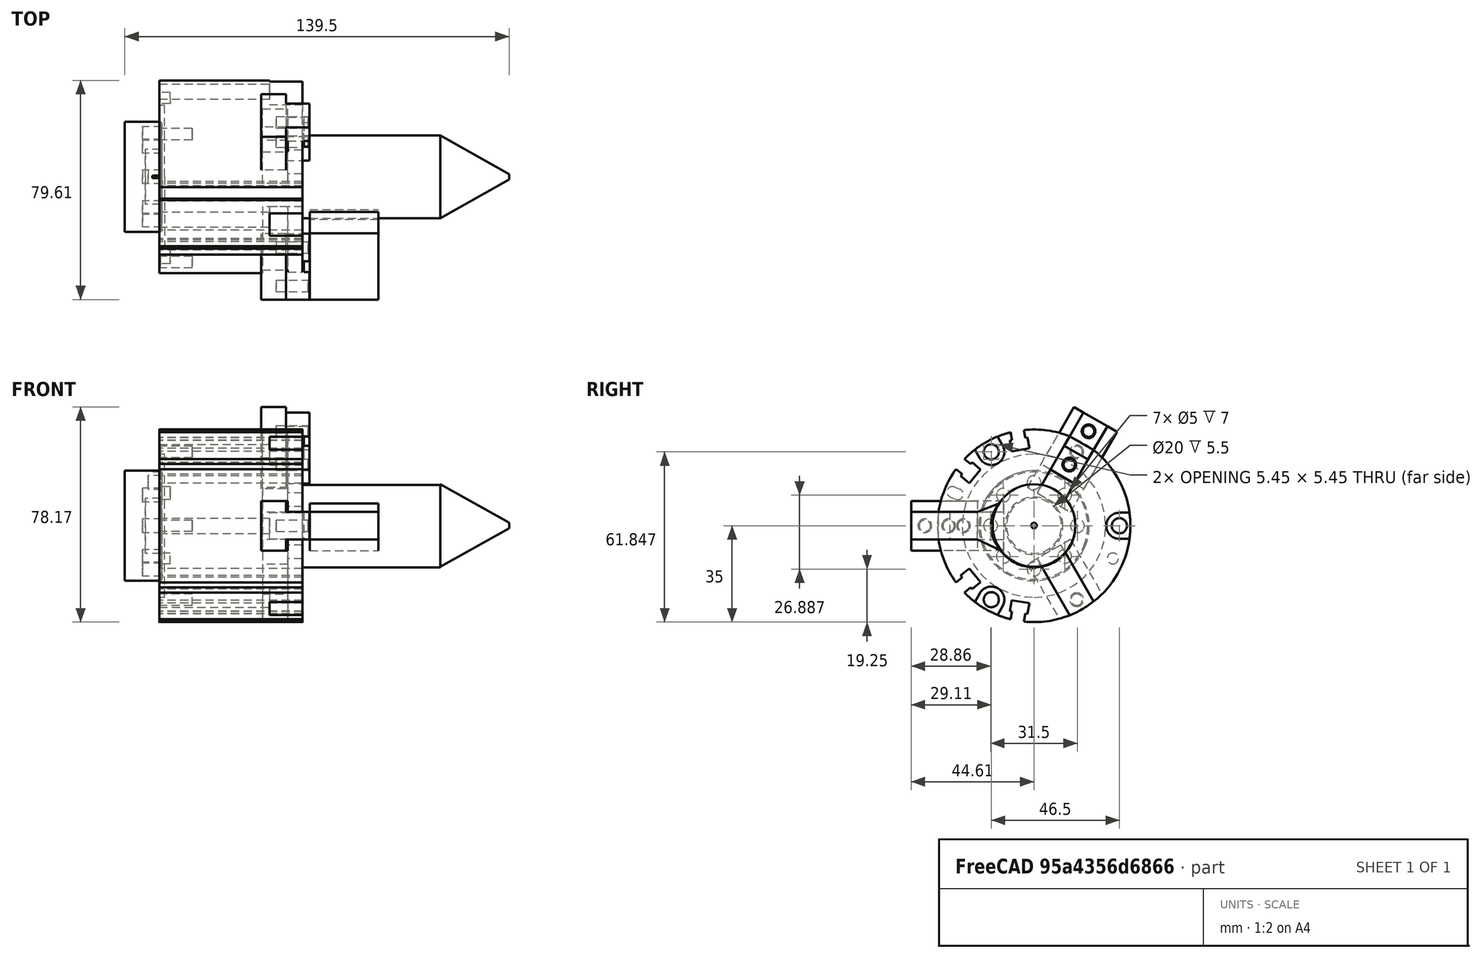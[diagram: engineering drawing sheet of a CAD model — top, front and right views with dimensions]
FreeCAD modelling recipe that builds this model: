
FCSTD DOCUMENT  (FreeCAD 0.19R24276 (Git))
Label: kuka_joint_6
License: All rights reserved
LicenseURL: http://en.wikipedia.org/wiki/All_rights_reserved
objects: Part::Feature×3, Part::FeaturePython×2, Sketcher::SketchObject×2, PartDesign::Pad×1, PartDesign::Body×1, Part::Cylinder×1, Part::Cone×1
note: 12 computed .brp shape members not serialized (recipe doc carries the construction recipe); baked Part::Feature solids carry a one-line shape summary decoded from their .brp

FEATURE [Part::Feature] Solid  label="KR6_KR10_R900_sixx_22"
  shape: bbox 13.5 x 40 x 40 mm, 26 faces (baked)
FEATURE [Part::Feature] Solid001  label="R1"
  Placement = pos=(576,0,890) rot=(0,1,0;1.5708rad)
  shape: bbox 52 x 70 x 70 mm, 102 faces (baked)
FEATURE [Part::Feature] Solid002  label="R2"
  Placement = pos=(570,4.8,881.7) rot=(0,1,0;1.5708rad)
  shape: bbox 17.5 x 27.59 x 29.78 mm, 24 faces (baked)
FEATURE [Part::FeaturePython] Clone  label="R003"  # Draft clone (typed FeaturePython)
  AttacherType = Attacher::AttachEngine3D
  Fuse = false
  Objects = -> [Solid002]
  Placement = pos=(570,4.80603,898.362) rot=(-0.654654,-0.377964,-0.654654;3.86433rad)
  Scale = (1,1,1)
FEATURE [Part::FeaturePython] Clone001  label="R004"  # Draft clone (typed FeaturePython)
  AttacherType = Attacher::AttachEngine3D
  Fuse = false
  Objects = -> [Solid002]
  Placement = pos=(570,-9.61321,890.021) rot=(0.654654,-0.377964,0.654654;3.86433rad)
  Scale = (1,1,1)
FEATURE [Sketcher::SketchObject] Sketch
  FullyConstrained = false
  MapMode = 5
  Placement = pos=(0,0,0) rot=(0.57735,0.57735,0.57735;2.0944rad)
  Support = -> [YZ_Plane]
  sketch-geometry (6):
    g0: LineSegment StartX=-44.5939 StartY=895.036 StartZ=0 EndX=-20.5483 EndY=895.036 EndZ=0
    g1: LineSegment StartX=-20.5483 StartY=885.006 StartZ=0 EndX=-44.5939 EndY=885.006 EndZ=0
    g2: LineSegment StartX=-44.5939 StartY=885.006 StartZ=0 EndX=-44.5939 EndY=895.036 EndZ=0
    g3: LineSegment StartX=-20.5483 StartY=895.036 StartZ=0 EndX=-12.7411 EndY=898.117 EndZ=0
    g4: LineSegment StartX=-20.5483 StartY=885.006 StartZ=0 EndX=-11.914 EndY=881.01 EndZ=0
    g5: ArcOfCircle CenterX=-2.73045 CenterY=890.027 CenterZ=0 NormalX=0 NormalY=0 NormalZ=1 AngleXU=0 Radius=12.8704 StartAngle=2.46196 EndAngle=3.91785
  constraints (9):
    c: Coincident(g1,g2)
    c: Coincident(g2,g0)
    c: Horizontal(g0)
    c: Horizontal(g1)
    c: Vertical(g2)
    c: Coincident(g3,g0)
    c: Coincident(g4,g1)
    c: Coincident(g5,g3)
    c: Coincident(g5,g4)
FEATURE [PartDesign::Pad] Pad
  Direction = (1,1,1)
  Length = 25
  Length2 = 100
  Placement = pos=(0,0,0) rot=(0.57735,0.57735,0.57735;2.0944rad)
  Profile = -> Sketch
  Type = 0
FEATURE [PartDesign::Body] Body
  Group = -> [Sketch,Pad]
  Origin = -> Origin
  Placement = pos=(578.6,0,0) rot=(0,0,1;0rad)
  Tip = -> Pad
FEATURE [Sketcher::SketchObject] Sketch001
  FullyConstrained = true
  MapMode = 2
  Placement = pos=(0,0,0) rot=(0.57735,0.57735,0.57735;2.0944rad)
  Support = -> [Pad]
FEATURE [Part::Cylinder] Cylinder
  Angle = 360
  AttacherType = Attacher::AttachEngine3D
  Height = 50
  Placement = pos=(576,-5.1e-15,889.9) rot=(0,1,0;1.5708rad)
  Radius = 15
FEATURE [Part::Cone] Cone
  Angle = 360
  AttacherType = Attacher::AttachEngine3D
  Height = 25
  Placement = pos=(651,0,890.1) rot=(0,1,0;4.71239rad)
  Radius1 = 1
  Radius2 = 15
